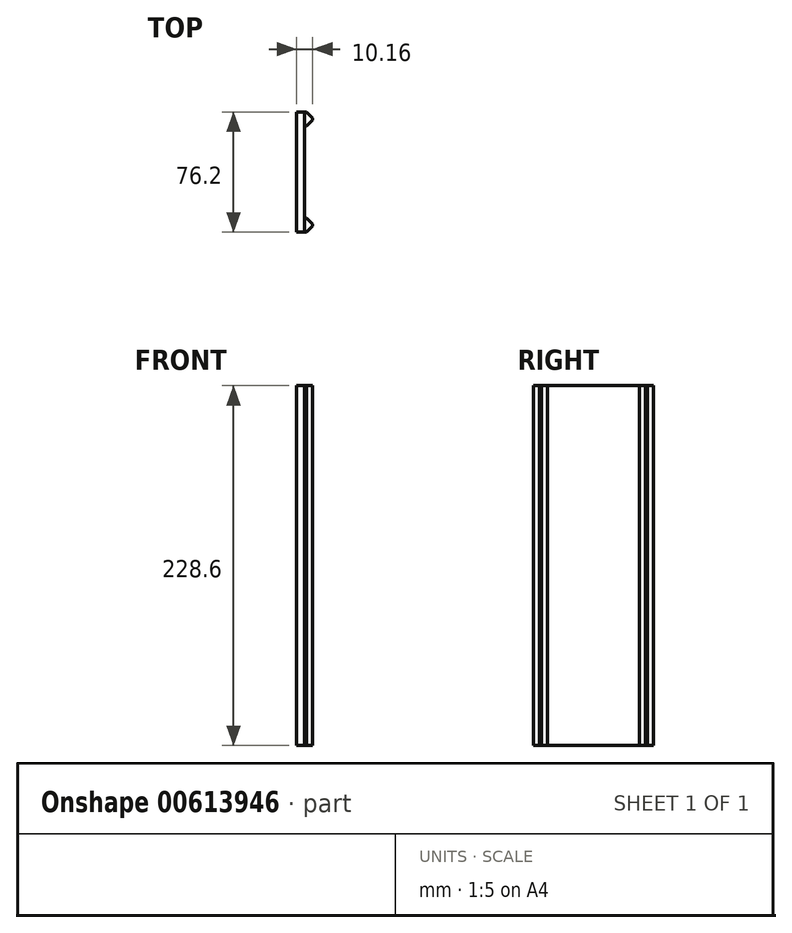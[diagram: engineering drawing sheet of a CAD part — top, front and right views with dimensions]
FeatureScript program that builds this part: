
annotation { "Feature Type Name" : "Feature", "Feature Type Description" : "" }
export const myFeature = defineFeature(function(context is Context, id is Id, definition is map)
    precondition{}
    {
        {
            var Q0;
            Q0=qCreatedBy(makeId("Right.planeOp"),FACE);
            var sketch = newSketch(context, id + "F0", { "sketchPlane" : qUnion([Q0])});
            skLineSegment(sketch, "E0.bottom", {"start": v(38.1, 114.3) * mm, "end": v(-38.1, 114.3) * mm});
            skLineSegment(sketch, "E0.top", {"start": v(38.1, -114.3) * mm, "end": v(-38.1, -114.3) * mm});
            skLineSegment(sketch, "E0.left", {"start": v(38.1, 114.3) * mm, "end": v(38.1, -114.3) * mm});
            skLineSegment(sketch, "E0.right", {"start": v(-38.1, 114.3) * mm, "end": v(-38.1, -114.3) * mm});
            skPoint(sketch, "E0.middle", {"position": v(0, 0) * mm});
            skSolve(sketch);
        }
        {
            var Q0;
            Q0=makeQuery(id+"F0.imprint","IMPRINT",FACE,{"disambiguationData":[TD([[makeQuery(id+"F0.imprint","IMPRINT",EDGE,{"derivedFrom":sQuery(id+"F0.wireOp",EDGE,"E0.bottom")}),1.0]])]});
            extrude(context, id + "F1", {"entities" : qUnion([Q0]), "depth" : 7.62 * mm, "offsetDistance" : 25.4 * mm});
        }
        {
            var Q0;
            Q0=makeQuery(id+"F1.opExtrude","CAP_FACE",FACE,{"disambiguationData":[OSD([sQuery(id+"F0.wireOp",EDGE,"E0.bottom"),sQuery(id+"F0.wireOp",EDGE,"E0.top"),sQuery(id+"F0.wireOp",EDGE,"E0.left"),sQuery(id+"F0.wireOp",EDGE,"E0.right")])],"isStart":false});
            var sketch = newSketch(context, id + "F2", { "sketchPlane" : qUnion([Q0])});
            skLineSegment(sketch, "E1.bottom", {"start": v(29.21, 114.3) * mm, "end": v(-29.21, 114.3) * mm});
            skLineSegment(sketch, "E1.top", {"start": v(29.21, -114.3) * mm, "end": v(-29.21, -114.3) * mm});
            skLineSegment(sketch, "E1.left", {"start": v(29.21, 114.3) * mm, "end": v(29.21, -114.3) * mm});
            skLineSegment(sketch, "E1.right", {"start": v(-29.21, 114.3) * mm, "end": v(-29.21, -114.3) * mm});
            skPoint(sketch, "E1.middle", {"position": v(0, 0) * mm});
            skSolve(sketch);
        }
        {
            var Q0;
            {var subQ0=sQuery(id+"F2.wireOp",EDGE,"E1.right");Q0=makeQuery(id+"F2.imprint","IMPRINT",FACE,{"disambiguationData":[TD([[makeQuery(id+"F2.imprint","IMPRINT",EDGE,{"derivedFrom":subQ0}),-1.0]])]});}
            var Q1;
            {var subQ0=sQuery(id+"F2.wireOp",EDGE,"E1.left");Q1=makeQuery(id+"F2.imprint","IMPRINT",FACE,{"disambiguationData":[TD([[makeQuery(id+"F2.imprint","IMPRINT",EDGE,{"derivedFrom":subQ0}),1.0]])]});}
            extrude(context, id + "F3", {"entities" : qUnion([Q0, Q1]), "depth" : 5.08 * mm, "offsetDistance" : 25.4 * mm});
        }
        {
            var Q0;
            Q0=makeQuery(id+"F3.opExtrude","CAP_EDGE",EDGE,{"disambiguationData":[OSD([sQuery(id+"F0.wireOp",EDGE,"E0.right")])],"isStart":false});
            var Q1;
            Q1=makeQuery(id+"F3.opExtrude","CAP_EDGE",EDGE,{"disambiguationData":[OSD([sQuery(id+"F2.wireOp",EDGE,"E1.right")])],"isStart":false});
            var Q2;
            Q2=makeQuery(id+"F3.opExtrude","CAP_EDGE",EDGE,{"disambiguationData":[OSD([sQuery(id+"F2.wireOp",EDGE,"E1.left")])],"isStart":false});
            var Q3;
            Q3=makeQuery(id+"F3.opExtrude","CAP_EDGE",EDGE,{"disambiguationData":[OSD([sQuery(id+"F0.wireOp",EDGE,"E0.left")])],"isStart":false});
            chamfer(context, id + "F4", {"entities" : qUnion([Q0, Q1, Q2, Q3]), "width" : 3.8 * mm, "tangentPropagation" : true});
        }
        {
            var Q0;
            Q0=makeQuery(id+"F1.opExtrude","CAP_FACE",FACE,{"disambiguationData":[OSD([sQuery(id+"F0.wireOp",EDGE,"E0.bottom"),sQuery(id+"F0.wireOp",EDGE,"E0.top"),sQuery(id+"F0.wireOp",EDGE,"E0.left"),sQuery(id+"F0.wireOp",EDGE,"E0.right")])],"isStart":true});
            extrude(context, id + "F5", {"entities" : qUnion([Q0]), "operationType" : NewBodyOperationType.REMOVE, "oppositeDirection" : true, "depth" : 2.54 * mm, "offsetDistance" : 25.4 * mm});
        }
    });
